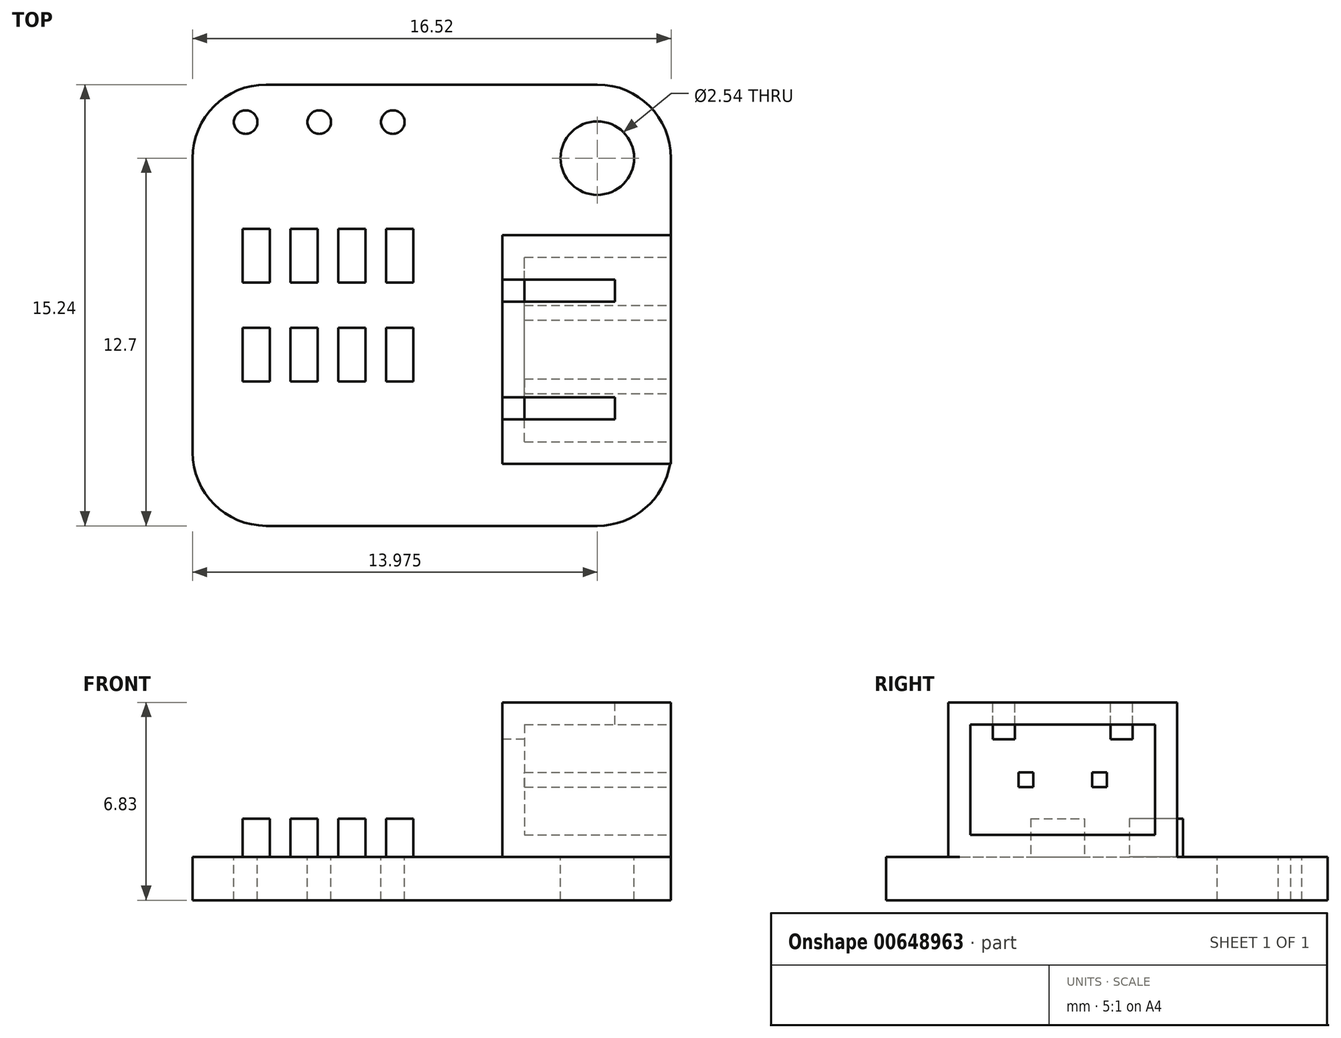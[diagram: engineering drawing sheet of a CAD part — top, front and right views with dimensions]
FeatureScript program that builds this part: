
annotation { "Feature Type Name" : "Feature", "Feature Type Description" : "" }
export const myFeature = defineFeature(function(context is Context, id is Id, definition is map)
    precondition{}
    {
        {
            var Q0;
            Q0=qCreatedBy(makeId("Top.planeOp"),FACE);
            var sketch = newSketch(context, id + "F0", { "sketchPlane" : qUnion([Q0])});
            skLineSegment(sketch, "E0.bottom", {"start": v(-8.26, -7.62) * mm, "end": v(8.26, -7.62) * mm});
            skLineSegment(sketch, "E0.top", {"start": v(-8.26, 7.62) * mm, "end": v(8.26, 7.62) * mm});
            skLineSegment(sketch, "E0.left", {"start": v(-8.26, -7.62) * mm, "end": v(-8.26, 7.62) * mm});
            skLineSegment(sketch, "E0.right", {"start": v(8.26, -7.62) * mm, "end": v(8.26, 7.62) * mm});
            skLineSegment(sketch, "E1", {"start": v(8.26, 7.62) * mm, "end": v(-8.26, -7.62) * mm, "construction": true});
            skSolve(sketch);
        }
        {
            var Q0;
            Q0 = qSketchRegion(id + "F0", true);
            extrude(context, id + "F1", {"entities" : qUnion([Q0]), "depth" : 1.5 * mm, "offsetDistance" : 25.4 * mm});
        }
        {
            var Q0;
            Q0=makeQuery(id+"F1.opExtrude","CAP_FACE",FACE,{"disambiguationData":[OSD([sQuery(id+"F0.wireOp",EDGE,"E0.bottom"),sQuery(id+"F0.wireOp",EDGE,"E0.top"),sQuery(id+"F0.wireOp",EDGE,"E0.left"),sQuery(id+"F0.wireOp",EDGE,"E0.right")])],"isStart":false});
            var sketch = newSketch(context, id + "F2", { "sketchPlane" : qUnion([Q0])});
            skCircle(sketch, "E2", {"center": v(5.72, 5.08) * mm, "radius": 1.27 * mm});
            skSolve(sketch);
        }
        {
            var Q0;
            Q0 = qSketchRegion(id + "F2", true);
            extrude(context, id + "F3", {"entities" : qUnion([Q0]), "operationType" : NewBodyOperationType.REMOVE, "endBound" : BoundingType.UP_TO_NEXT, "oppositeDirection" : true, "depth" : 25.4 * mm, "offsetDistance" : 25.4 * mm});
        }
        {
            var Q0;
            Q0=makeQuery(id+"F1.opExtrude","SWEPT_EDGE",EDGE,{"disambiguationData":[OSD([sQuery(id+"F0.wireOp",EDGE,"E0.bottom"),sQuery(id+"F0.wireOp",EDGE,"E0.right")])]});
            var Q1;
            Q1=makeQuery(id+"F1.opExtrude","SWEPT_EDGE",EDGE,{"disambiguationData":[OSD([sQuery(id+"F0.wireOp",EDGE,"E0.top"),sQuery(id+"F0.wireOp",EDGE,"E0.right")])]});
            var Q2;
            Q2=makeQuery(id+"F1.opExtrude","SWEPT_EDGE",EDGE,{"disambiguationData":[OSD([sQuery(id+"F0.wireOp",EDGE,"E0.bottom"),sQuery(id+"F0.wireOp",EDGE,"E0.left")])]});
            var Q3;
            Q3=makeQuery(id+"F1.opExtrude","SWEPT_EDGE",EDGE,{"disambiguationData":[OSD([sQuery(id+"F0.wireOp",EDGE,"E0.top"),sQuery(id+"F0.wireOp",EDGE,"E0.left")])]});
            fillet(context, id + "F4", {"entities" : qUnion([Q0, Q1, Q2, Q3]), "radius" : 2.54 * mm, "tangentPropagation" : true, "allowEdgeOverflow" : false});
        }
        {
            var Q0;
            Q0=makeQuery(id+"F1.opExtrude","CAP_FACE",FACE,{"disambiguationData":[OSD([sQuery(id+"F0.wireOp",EDGE,"E0.bottom"),sQuery(id+"F0.wireOp",EDGE,"E0.top"),sQuery(id+"F0.wireOp",EDGE,"E0.left"),sQuery(id+"F0.wireOp",EDGE,"E0.right")])],"isStart":false});
            var sketch = newSketch(context, id + "F5", { "sketchPlane" : qUnion([Q0])});
            skLineSegment(sketch, "E3.bottom", {"start": v(2.44, -5.47) * mm, "end": v(8.26, -5.47) * mm});
            skLineSegment(sketch, "E3.top", {"start": v(2.44, 2.43) * mm, "end": v(8.26, 2.43) * mm});
            skLineSegment(sketch, "E3.left", {"start": v(2.44, -5.47) * mm, "end": v(2.44, 2.43) * mm});
            skLineSegment(sketch, "E3.right", {"start": v(8.26, -5.47) * mm, "end": v(8.26, 2.43) * mm});
            skLineSegment(sketch, "E4", {"start": v(8.26, -1.52) * mm, "end": v(2.44, -1.52) * mm, "construction": true});
            skSolve(sketch);
        }
        {
            var Q0;
            Q0 = qSketchRegion(id + "F5", true);
            extrude(context, id + "F6", {"entities" : qUnion([Q0]), "operationType" : NewBodyOperationType.ADD, "depth" : 5.33 * mm, "offsetDistance" : 25.4 * mm});
        }
        {
            var Q0;
            Q0=makeQuery(id+"F6.opExtrude","SWEPT_FACE",FACE,{"disambiguationData":[OSD([sQuery(id+"F5.wireOp",EDGE,"E3.right")])]});
            var sketch = newSketch(context, id + "F7", { "sketchPlane" : qUnion([Q0])});
            skLineSegment(sketch, "E5.0", {"start": v(-4.71, 6.07) * mm, "end": v(-4.71, 2.26) * mm});
            skLineSegment(sketch, "E5.1", {"start": v(-4.71, 6.07) * mm, "end": v(1.66, 6.07) * mm});
            skLineSegment(sketch, "E5.2", {"start": v(1.66, 6.07) * mm, "end": v(1.66, 2.26) * mm});
            skLineSegment(sketch, "E6", {"start": v(-4.71, 2.26) * mm, "end": v(1.66, 2.26) * mm});
            skLineSegment(sketch, "E7", {"start": v(-4.71, 2.26) * mm, "end": v(1.66, 6.07) * mm, "construction": true});
            skLineSegment(sketch, "E8", {"start": v(-1.52, 4.17) * mm, "end": v(-1.52, 2.26) * mm, "construction": true});
            skLineSegment(sketch, "E9.bottom", {"start": v(-2.54, 3.91) * mm, "end": v(-3.05, 3.91) * mm});
            skLineSegment(sketch, "E9.top", {"start": v(-2.54, 4.42) * mm, "end": v(-3.05, 4.42) * mm});
            skLineSegment(sketch, "E9.left", {"start": v(-2.54, 3.91) * mm, "end": v(-2.54, 4.42) * mm});
            skLineSegment(sketch, "E9.right", {"start": v(-3.05, 3.91) * mm, "end": v(-3.05, 4.42) * mm});
            skPoint(sketch, "E9.middle", {"position": v(-2.8, 4.17) * mm});
            skLineSegment(sketch, "E10.MirrorCS", {"start": v(-0.5, 3.91) * mm, "end": v(-0.5, 4.42) * mm});
            skLineSegment(sketch, "E11.MirrorCS", {"start": v(-0.5, 4.42) * mm, "end": v(0, 4.42) * mm});
            skLineSegment(sketch, "E12.MirrorCS", {"start": v(0, 3.91) * mm, "end": v(0, 4.42) * mm});
            skLineSegment(sketch, "E13.MirrorCS", {"start": v(-0.5, 3.91) * mm, "end": v(0, 3.91) * mm});
            skSolve(sketch);
        }
        {
            var Q0;
            Q0 = qSketchRegion(id + "F7", true);
            var Q1;
            Q1=makeQuery(id+"F6.opExtrude","SWEPT_FACE",FACE,{"disambiguationData":[OSD([sQuery(id+"F5.wireOp",EDGE,"E3.left")])]});
            extrude(context, id + "F8", {"entities" : qUnion([Q0]), "operationType" : NewBodyOperationType.REMOVE, "endBound" : BoundingType.UP_TO_SURFACE, "oppositeDirection" : true, "depth" : 25.4 * mm, "endBoundEntityFace" : qUnion([Q1]), "hasOffset" : true, "offsetDistance" : 0.76 * mm});
        }
        {
            var Q0;
            Q0=makeQuery(id+"F6.opExtrude","CAP_FACE",FACE,{"disambiguationData":[OSD([sQuery(id+"F5.wireOp",EDGE,"E3.bottom"),sQuery(id+"F5.wireOp",EDGE,"E3.top"),sQuery(id+"F5.wireOp",EDGE,"E3.left"),sQuery(id+"F5.wireOp",EDGE,"E3.right")])],"isStart":false});
            var sketch = newSketch(context, id + "F9", { "sketchPlane" : qUnion([Q0])});
            skLineSegment(sketch, "E14.bottom", {"start": v(6.32, 0.13) * mm, "end": v(2.44, 0.13) * mm});
            skLineSegment(sketch, "E14.top", {"start": v(6.32, 0.89) * mm, "end": v(2.44, 0.89) * mm});
            skLineSegment(sketch, "E14.left", {"start": v(6.32, 0.13) * mm, "end": v(6.32, 0.89) * mm});
            skLineSegment(sketch, "E14.right", {"start": v(2.44, 0.13) * mm, "end": v(2.44, 0.89) * mm});
            skPoint(sketch, "E14.middle", {"position": v(4.38, 0.5) * mm});
            skLineSegment(sketch, "E15", {"start": v(8.26, -1.52) * mm, "end": v(13.87, -1.52) * mm, "construction": true});
            skLineSegment(sketch, "E16.MirrorCS", {"start": v(6.32, -3.94) * mm, "end": v(2.44, -3.94) * mm});
            skLineSegment(sketch, "E17.MirrorCS", {"start": v(2.44, -3.18) * mm, "end": v(2.44, -3.94) * mm});
            skLineSegment(sketch, "E18.MirrorCS", {"start": v(6.32, -3.18) * mm, "end": v(2.44, -3.18) * mm});
            skLineSegment(sketch, "E19.MirrorCS", {"start": v(6.32, -3.18) * mm, "end": v(6.32, -3.94) * mm});
            skSolve(sketch);
        }
        {
            var Q0;
            Q0 = qSketchRegion(id + "F9", true);
            extrude(context, id + "F10", {"entities" : qUnion([Q0]), "operationType" : NewBodyOperationType.REMOVE, "oppositeDirection" : true, "depth" : 1.27 * mm, "offsetDistance" : 25.4 * mm});
        }
        {
            var Q0;
            Q0=makeQuery(id+"F1.opExtrude","CAP_FACE",FACE,{"disambiguationData":[OSD([sQuery(id+"F0.wireOp",EDGE,"E0.bottom"),sQuery(id+"F0.wireOp",EDGE,"E0.top"),sQuery(id+"F0.wireOp",EDGE,"E0.left"),sQuery(id+"F0.wireOp",EDGE,"E0.right")])],"isStart":false});
            var sketch = newSketch(context, id + "F11", { "sketchPlane" : qUnion([Q0])});
            skCircle(sketch, "E20", {"center": v(-6.43, 6.32) * mm, "radius": 0.4 * mm});
            skCircle(sketch, "E21.1.0.0", {"center": v(-3.89, 6.32) * mm, "radius": 0.4 * mm});
            skCircle(sketch, "E21.2.0.0", {"center": v(-1.35, 6.32) * mm, "radius": 0.4 * mm});
            skLineSegment(sketch, "E21.direction1", {"start": v(-6.43, 6.32) * mm, "end": v(-3.89, 6.32) * mm, "construction": true});
            skSolve(sketch);
        }
        {
            var Q0;
            Q0 = qSketchRegion(id + "F11", true);
            extrude(context, id + "F12", {"entities" : qUnion([Q0]), "operationType" : NewBodyOperationType.REMOVE, "endBound" : BoundingType.UP_TO_NEXT, "oppositeDirection" : true, "depth" : 25.4 * mm, "offsetDistance" : 25.4 * mm});
        }
        {
            var Q0;
            Q0=makeQuery(id+"F1.opExtrude","CAP_FACE",FACE,{"disambiguationData":[OSD([sQuery(id+"F0.wireOp",EDGE,"E0.bottom"),sQuery(id+"F0.wireOp",EDGE,"E0.top"),sQuery(id+"F0.wireOp",EDGE,"E0.left"),sQuery(id+"F0.wireOp",EDGE,"E0.right")])],"isStart":false});
            var sketch = newSketch(context, id + "F13", { "sketchPlane" : qUnion([Q0])});
            skLineSegment(sketch, "E22.bottom", {"start": v(-6.53, 2.63) * mm, "end": v(-5.6, 2.63) * mm});
            skLineSegment(sketch, "E22.top", {"start": v(-6.53, 0.78) * mm, "end": v(-5.6, 0.78) * mm});
            skLineSegment(sketch, "E22.left", {"start": v(-6.53, 2.63) * mm, "end": v(-6.53, 0.78) * mm});
            skLineSegment(sketch, "E22.right", {"start": v(-5.6, 2.63) * mm, "end": v(-5.6, 0.78) * mm});
            skLineSegment(sketch, "E23.1.0.0", {"start": v(-3.94, 2.63) * mm, "end": v(-3.94, 0.78) * mm});
            skLineSegment(sketch, "E23.1.0.1", {"start": v(-4.88, 2.63) * mm, "end": v(-4.88, 0.78) * mm});
            skLineSegment(sketch, "E23.1.0.2", {"start": v(-4.88, 2.63) * mm, "end": v(-3.94, 2.63) * mm});
            skLineSegment(sketch, "E23.1.0.3", {"start": v(-4.88, 0.78) * mm, "end": v(-3.94, 0.78) * mm});
            skLineSegment(sketch, "E23.2.0.0", {"start": v(-2.3, 2.63) * mm, "end": v(-2.3, 0.78) * mm});
            skLineSegment(sketch, "E23.2.0.1", {"start": v(-3.23, 2.63) * mm, "end": v(-3.23, 0.78) * mm});
            skLineSegment(sketch, "E23.2.0.2", {"start": v(-3.23, 2.63) * mm, "end": v(-2.3, 2.63) * mm});
            skLineSegment(sketch, "E23.2.0.3", {"start": v(-3.23, 0.78) * mm, "end": v(-2.3, 0.78) * mm});
            skLineSegment(sketch, "E23.direction1", {"start": v(-6.53, 0.78) * mm, "end": v(-4.88, 0.78) * mm, "construction": true});
            skLineSegment(sketch, "E24.0.3.0", {"start": v(-0.64, 2.63) * mm, "end": v(-0.64, 0.78) * mm});
            skLineSegment(sketch, "E24.3.3.0", {"start": v(-1.58, 2.63) * mm, "end": v(-1.58, 0.78) * mm});
            skLineSegment(sketch, "E24.6.3.0", {"start": v(-1.58, 2.63) * mm, "end": v(-0.64, 2.63) * mm});
            skLineSegment(sketch, "E24.9.3.0", {"start": v(-1.58, 0.78) * mm, "end": v(-0.64, 0.78) * mm});
            skLineSegment(sketch, "E25", {"start": v(0, 0) * mm, "end": v(0.66, 0) * mm, "construction": true});
            skLineSegment(sketch, "E26.MirrorCS", {"start": v(-6.53, -0.78) * mm, "end": v(-5.6, -0.78) * mm});
            skLineSegment(sketch, "E27.MirrorCS", {"start": v(-0.64, -2.63) * mm, "end": v(-0.64, -0.78) * mm});
            skLineSegment(sketch, "E28.MirrorCS", {"start": v(-1.58, -2.63) * mm, "end": v(-1.58, -0.78) * mm});
            skLineSegment(sketch, "E29.MirrorCS", {"start": v(-1.58, -2.63) * mm, "end": v(-0.64, -2.63) * mm});
            skLineSegment(sketch, "E30.MirrorCS", {"start": v(-6.53, -2.63) * mm, "end": v(-5.6, -2.63) * mm});
            skLineSegment(sketch, "E31.MirrorCS", {"start": v(-6.53, -2.63) * mm, "end": v(-6.53, -0.78) * mm});
            skLineSegment(sketch, "E32.MirrorCS", {"start": v(-5.6, -2.63) * mm, "end": v(-5.6, -0.78) * mm});
            skLineSegment(sketch, "E33.MirrorCS", {"start": v(-3.94, -2.63) * mm, "end": v(-3.94, -0.78) * mm});
            skLineSegment(sketch, "E34.MirrorCS", {"start": v(-4.88, -2.63) * mm, "end": v(-4.88, -0.78) * mm});
            skLineSegment(sketch, "E35.MirrorCS", {"start": v(-4.88, -2.63) * mm, "end": v(-3.94, -2.63) * mm});
            skLineSegment(sketch, "E36.MirrorCS", {"start": v(-4.88, -0.78) * mm, "end": v(-3.94, -0.78) * mm});
            skLineSegment(sketch, "E37.MirrorCS", {"start": v(-2.3, -2.63) * mm, "end": v(-2.3, -0.78) * mm});
            skLineSegment(sketch, "E38.MirrorCS", {"start": v(-6.53, -0.78) * mm, "end": v(-4.88, -0.78) * mm, "construction": true});
            skLineSegment(sketch, "E39.MirrorCS", {"start": v(-3.23, -0.78) * mm, "end": v(-2.3, -0.78) * mm});
            skLineSegment(sketch, "E40.MirrorCS", {"start": v(-1.58, -0.78) * mm, "end": v(-0.64, -0.78) * mm});
            skLineSegment(sketch, "E41.MirrorCS", {"start": v(-3.23, -2.63) * mm, "end": v(-2.3, -2.63) * mm});
            skLineSegment(sketch, "E42.MirrorCS", {"start": v(-3.23, -2.63) * mm, "end": v(-3.23, -0.78) * mm});
            skSolve(sketch);
        }
        {
            var Q0;
            Q0 = qSketchRegion(id + "F13", true);
            extrude(context, id + "F14", {"entities" : qUnion([Q0]), "operationType" : NewBodyOperationType.ADD, "depth" : 1.32 * mm, "offsetDistance" : 25.4 * mm});
        }
    });
